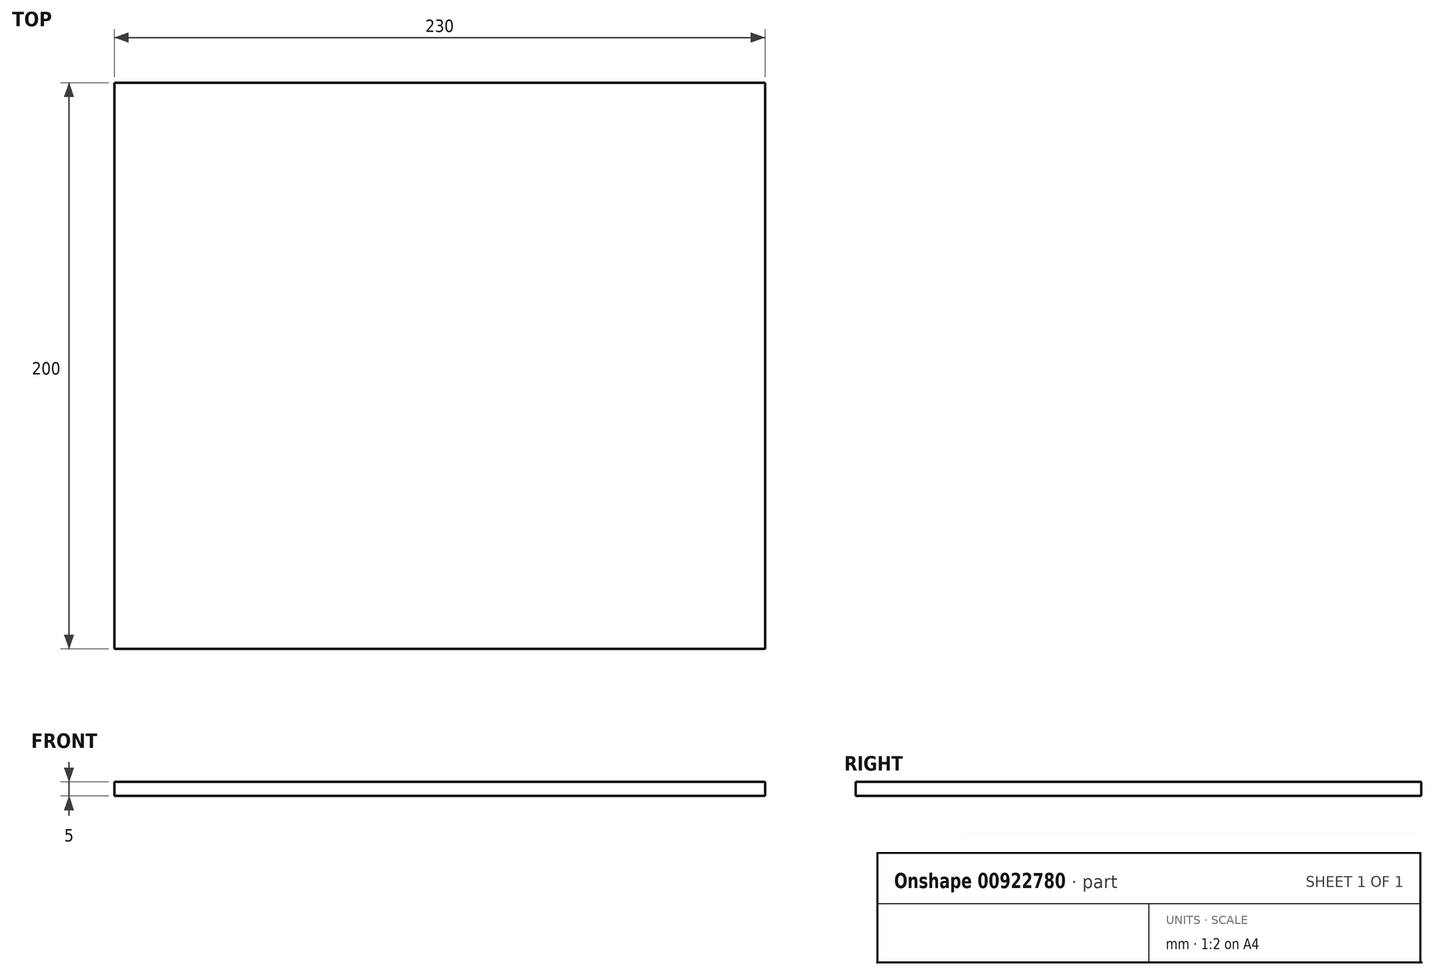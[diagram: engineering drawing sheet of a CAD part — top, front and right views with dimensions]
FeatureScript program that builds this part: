
annotation { "Feature Type Name" : "Feature", "Feature Type Description" : "" }
export const myFeature = defineFeature(function(context is Context, id is Id, definition is map)
    precondition{}
    {
        {
            var Q0;
            Q0=qCreatedBy(makeId("Top.planeOp"),FACE);
            var sketch = newSketch(context, id + "F0", { "sketchPlane" : qUnion([Q0])});
            skLineSegment(sketch, "E0.bottom", {"start": v(-115, 100) * mm, "end": v(115, 100) * mm});
            skLineSegment(sketch, "E0.top", {"start": v(-115, -100) * mm, "end": v(115, -100) * mm});
            skLineSegment(sketch, "E0.left", {"start": v(-115, 100) * mm, "end": v(-115, -100) * mm});
            skLineSegment(sketch, "E0.right", {"start": v(115, 100) * mm, "end": v(115, -100) * mm});
            skSolve(sketch);
        }
        {
            var Q0;
            Q0=makeQuery(id+"F0.imprint","IMPRINT",FACE,{"disambiguationData":[TD([[makeQuery(id+"F0.imprint","IMPRINT",EDGE,{"derivedFrom":sQuery(id+"F0.wireOp",EDGE,"E0.bottom")}),-1.0]])]});
            extrude(context, id + "F1", {"entities" : qUnion([Q0]), "depth" : 5 * mm, "offsetDistance" : 25 * mm});
        }
    });
